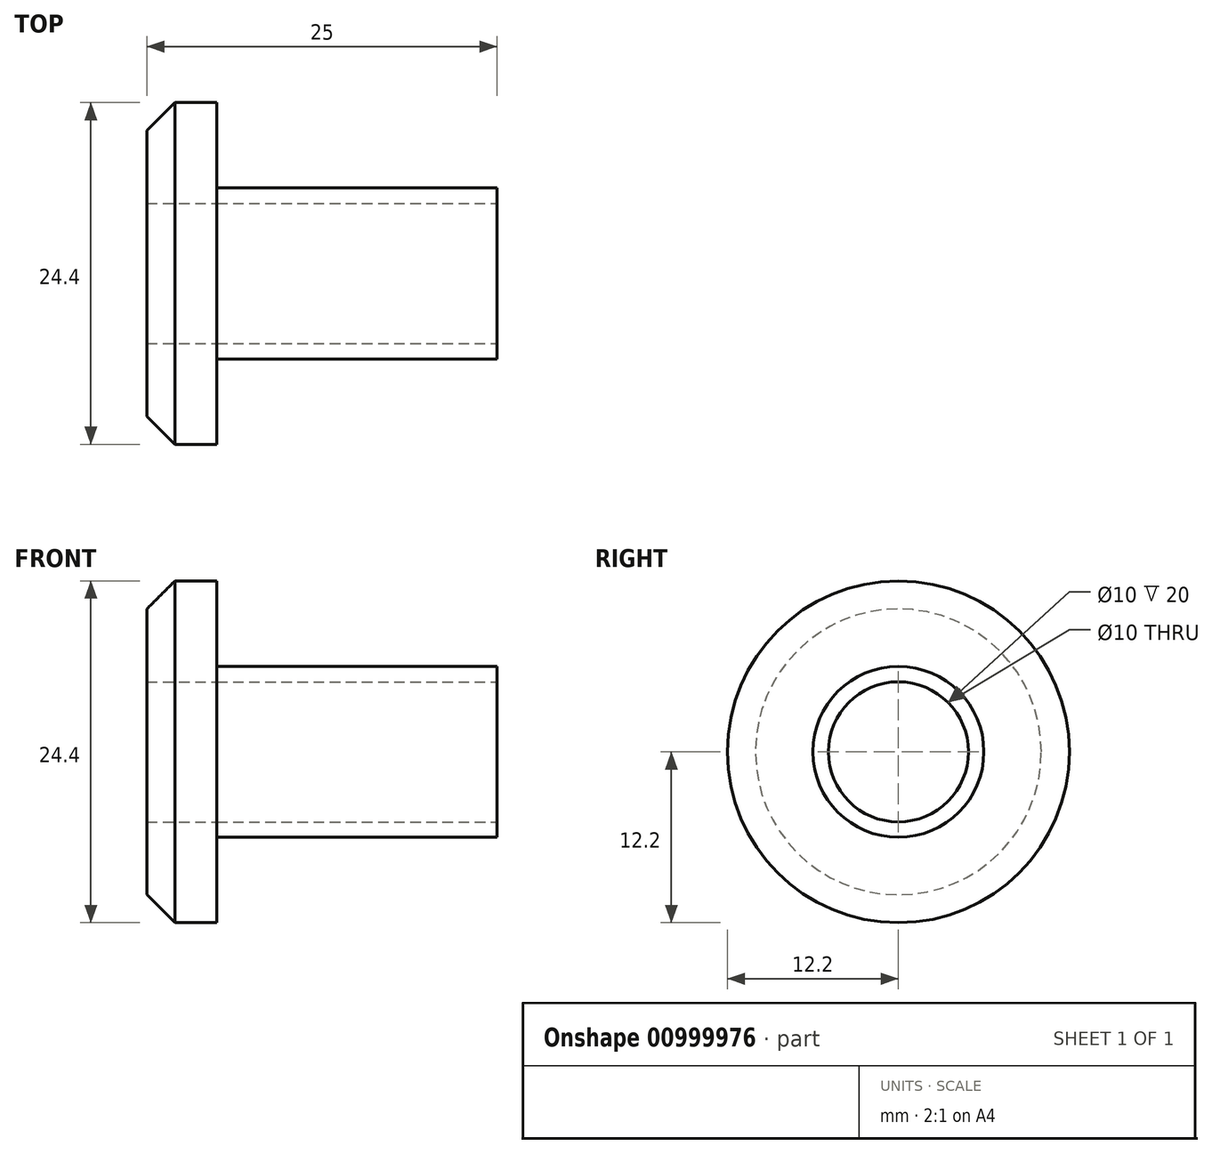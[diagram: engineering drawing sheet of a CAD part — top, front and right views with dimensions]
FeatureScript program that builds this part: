
annotation { "Feature Type Name" : "Feature", "Feature Type Description" : "" }
export const myFeature = defineFeature(function(context is Context, id is Id, definition is map)
    precondition{}
    {
        {
            var Q0;
            Q0=qCreatedBy(makeId("Front.planeOp"),FACE);
            var sketch = newSketch(context, id + "F0", { "sketchPlane" : qUnion([Q0])});
            skLineSegment(sketch, "E0.bottom", {"start": v(0, 0) * mm, "end": v(20, 0) * mm});
            skLineSegment(sketch, "E0.top", {"start": v(0, 6.1) * mm, "end": v(20, 6.1) * mm});
            skLineSegment(sketch, "E0.left", {"start": v(0, 0) * mm, "end": v(0, 6.1) * mm});
            skLineSegment(sketch, "E0.right", {"start": v(20, 0) * mm, "end": v(20, 6.1) * mm});
            skSolve(sketch);
        }
        {
            var Q0;
            Q0=qCreatedBy(makeId("Front.planeOp"),FACE);
            var sketch = newSketch(context, id + "F1", { "sketchPlane" : qUnion([Q0])});
            skLineSegment(sketch, "E1.bottom", {"start": v(0, 0) * mm, "end": v(-5, 0) * mm});
            skLineSegment(sketch, "E1.top", {"start": v(0, 12.2) * mm, "end": v(-5, 12.2) * mm});
            skLineSegment(sketch, "E1.left", {"start": v(0, 0) * mm, "end": v(0, 12.2) * mm});
            skLineSegment(sketch, "E1.right", {"start": v(-5, 0) * mm, "end": v(-5, 12.2) * mm});
            skSolve(sketch);
        }
        {
            var Q0;
            Q0=qCreatedBy(makeId("Front.planeOp"),FACE);
            var sketch = newSketch(context, id + "F2", { "sketchPlane" : qUnion([Q0])});
            skLineSegment(sketch, "E2", {"start": v(-33.59, 0) * mm, "end": v(35.22, 0) * mm, "construction": true});
            skSolve(sketch);
        }
        {
            var Q0;
            Q0=makeQuery(id+"F1.imprint","IMPRINT",FACE,{"disambiguationData":[TD([[makeQuery(id+"F1.imprint","IMPRINT",EDGE,{"derivedFrom":sQuery(id+"F1.wireOp",EDGE,"E1.bottom")}),-1.0]])]});
            var Q1;
            Q1=makeQuery(id+"F0.imprint","IMPRINT",FACE,{"disambiguationData":[TD([[makeQuery(id+"F0.imprint","IMPRINT",EDGE,{"derivedFrom":sQuery(id+"F0.wireOp",EDGE,"E0.bottom")}),1.0]])]});
            var Q2;
            Q2=sQuery(id+"F2.wireOp",EDGE,"E2");
            revolve(context, id + "F3", {"surfaceOperationType" : NewSurfaceOperationType.NEW, "entities" : qUnion([Q0, Q1]), "axis" : qUnion([Q2]), "revolveType" : RevolveType.FULL});
        }
        {
            var Q0;
            Q0=makeQuery(id+"F3.opRevolve","SWEPT_FACE",FACE,{"disambiguationData":[OSD([sQuery(id+"F0.wireOp",EDGE,"E0.right")])]});
            var sketch = newSketch(context, id + "F4", { "sketchPlane" : qUnion([Q0])});
            skCircle(sketch, "E3", {"center": v(0, 0) * mm, "radius": 5 * mm});
            skSolve(sketch);
        }
        {
            var Q0;
            Q0=makeQuery(id+"F4.imprint","IMPRINT",FACE,{"disambiguationData":[TD([[makeQuery(id+"F4.imprint","IMPRINT",EDGE,{"derivedFrom":sQuery(id+"F4.wireOp",EDGE,"E3")}),1.0]])]});
            var Q1;
            Q1=makeQuery(id+"F3.opRevolve","SWEPT_FACE",FACE,{"disambiguationData":[OSD([sQuery(id+"F1.wireOp",EDGE,"E1.right")])]});
            extrude(context, id + "F5", {"entities" : qUnion([Q0]), "operationType" : NewBodyOperationType.REMOVE, "endBound" : BoundingType.UP_TO_SURFACE, "oppositeDirection" : true, "depth" : 25 * mm, "endBoundEntityFace" : qUnion([Q1]), "offsetDistance" : 25 * mm});
        }
        {
            var Q0;
            Q0=makeQuery(id+"F3.opRevolve","SWEPT_EDGE",EDGE,{"disambiguationData":[OSD([sQuery(id+"F1.wireOp",EDGE,"E1.top"),sQuery(id+"F1.wireOp",EDGE,"E1.right")])]});
            chamfer(context, id + "F6", {"entities" : qUnion([Q0]), "width" : 2 * mm, "tangentPropagation" : true});
        }
    });
